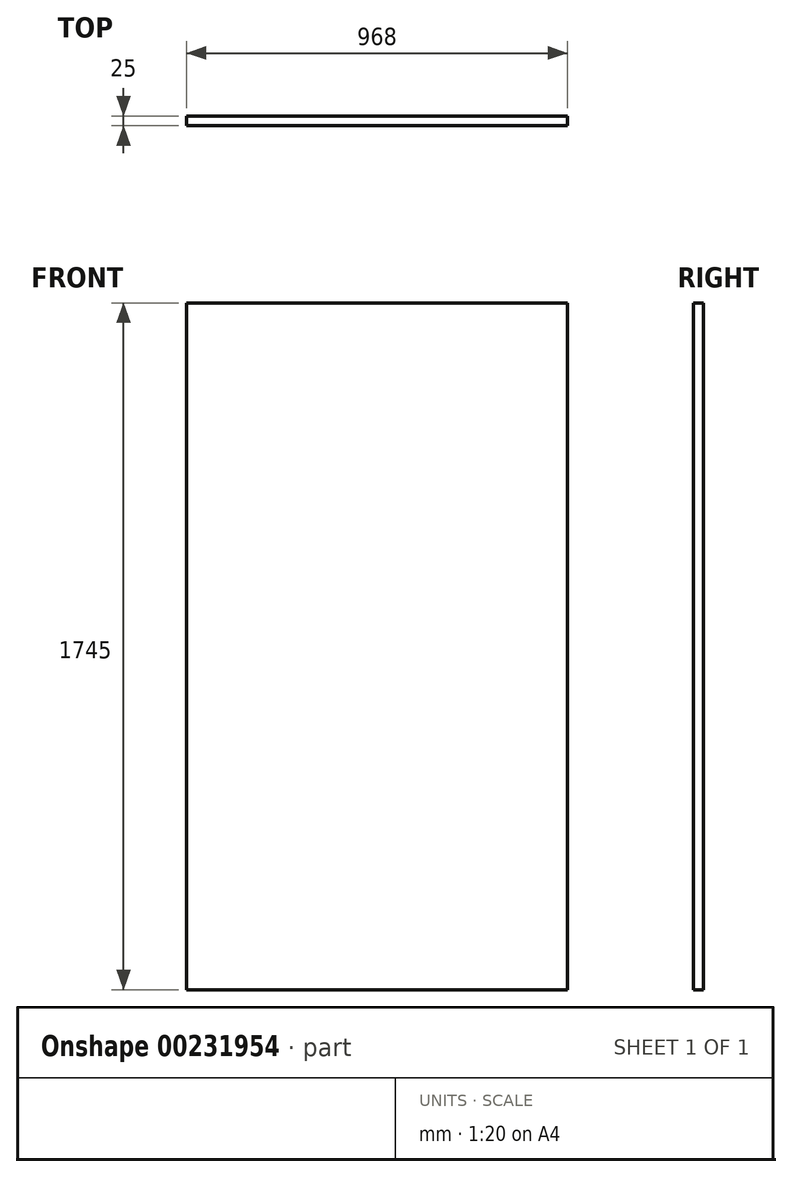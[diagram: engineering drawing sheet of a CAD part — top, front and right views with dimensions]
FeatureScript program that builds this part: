
annotation { "Feature Type Name" : "Feature", "Feature Type Description" : "" }
export const myFeature = defineFeature(function(context is Context, id is Id, definition is map)
    precondition{}
    {
        {
            var Q0;
            Q0=qCreatedBy(makeId("Front.planeOp"),FACE);
            var sketch = newSketch(context, id + "F0", { "sketchPlane" : qUnion([Q0])});
            skLineSegment(sketch, "E0.bottom", {"start": v(-484, 872.5) * mm, "end": v(484, 872.5) * mm});
            skLineSegment(sketch, "E0.top", {"start": v(-484, -872.5) * mm, "end": v(484, -872.5) * mm});
            skLineSegment(sketch, "E0.left", {"start": v(-484, 872.5) * mm, "end": v(-484, -872.5) * mm});
            skLineSegment(sketch, "E0.right", {"start": v(484, 872.5) * mm, "end": v(484, -872.5) * mm});
            skPoint(sketch, "E0.middle", {"position": v(0, 0) * mm});
            skSolve(sketch);
        }
        {
            var Q0;
            Q0 = qSketchRegion(id + "F0", true);
            extrude(context, id + "F1", {"entities" : qUnion([Q0]), "depth" : 25 * mm});
        }
    });
